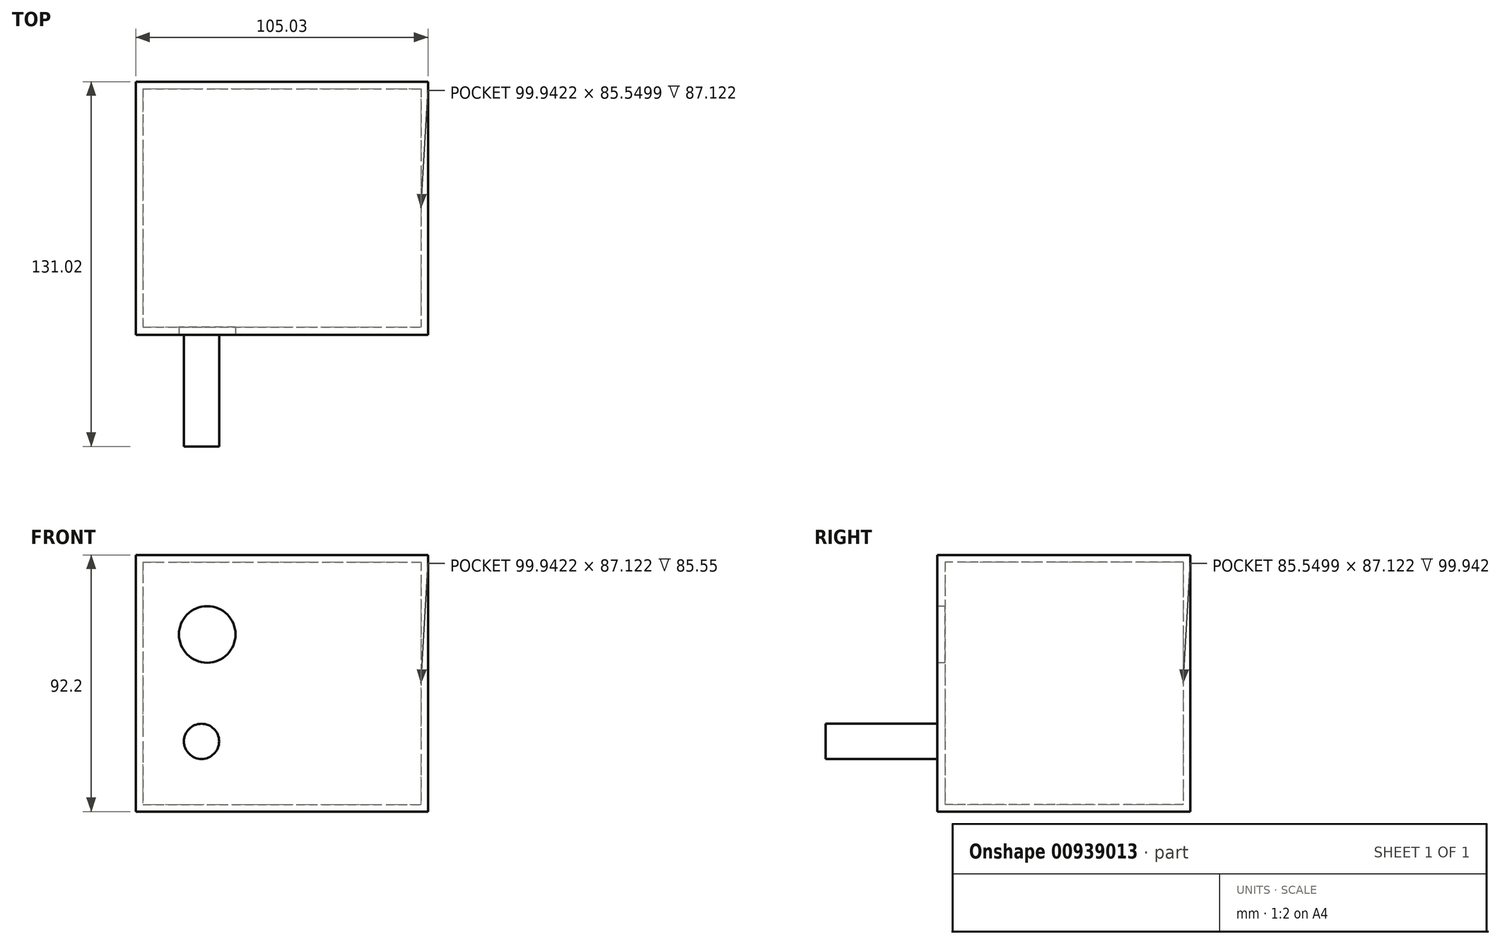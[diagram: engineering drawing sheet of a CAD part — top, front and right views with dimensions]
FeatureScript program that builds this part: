
annotation { "Feature Type Name" : "Feature", "Feature Type Description" : "" }
export const myFeature = defineFeature(function(context is Context, id is Id, definition is map)
    precondition{}
    {
        {
            var Q0;
            Q0=qCreatedBy(makeId("Top.planeOp"),FACE);
            var sketch = newSketch(context, id + "F0", { "sketchPlane" : qUnion([Q0])});
            skLineSegment(sketch, "E0.bottom", {"start": v(-76.02, 23.42) * mm, "end": v(29, 23.42) * mm});
            skLineSegment(sketch, "E0.top", {"start": v(-76.02, -67.46) * mm, "end": v(29, -67.46) * mm});
            skLineSegment(sketch, "E0.left", {"start": v(-76.02, 23.42) * mm, "end": v(-76.02, -67.46) * mm});
            skLineSegment(sketch, "E0.right", {"start": v(29, 23.42) * mm, "end": v(29, -67.46) * mm});
            skSolve(sketch);
        }
        {
            var Q0;
            Q0=makeQuery(id+"F0.imprint","IMPRINT",FACE,{"disambiguationData":[TD([[makeQuery(id+"F0.imprint","IMPRINT",EDGE,{"derivedFrom":sQuery(id+"F0.wireOp",EDGE,"E0.bottom")}),-1.0]])]});
            extrude(context, id + "F1", {"entities" : qUnion([Q0]), "depth" : 92.2 * mm, "offsetDistance" : 25.4 * mm});
        }
        {
            var Q0;
            Q0=makeQuery(id+"F1.opExtrude","SWEPT_FACE",FACE,{"disambiguationData":[OSD([sQuery(id+"F0.wireOp",EDGE,"E0.top")])]});
            shell(context, id + "F2", {"entities" : qUnion([Q0]), "thickness" : 2.54 * mm});
        }
        {
            var Q0;
            Q0=makeQuery(id+"F1.opExtrude","SWEPT_FACE",FACE,{"disambiguationData":[OSD([sQuery(id+"F0.wireOp",EDGE,"E0.top")])]});
            var sketch = newSketch(context, id + "F3", { "sketchPlane" : qUnion([Q0])});
            skLineSegment(sketch, "E1.bottom", {"start": v(-73.48, 89.66) * mm, "end": v(26.47, 89.66) * mm});
            skLineSegment(sketch, "E1.top", {"start": v(-73.48, 2.54) * mm, "end": v(26.47, 2.54) * mm});
            skLineSegment(sketch, "E1.left", {"start": v(-73.48, 89.66) * mm, "end": v(-73.48, 2.54) * mm});
            skLineSegment(sketch, "E1.right", {"start": v(26.47, 89.66) * mm, "end": v(26.47, 2.54) * mm});
            skSolve(sketch);
        }
        {
            var Q0;
            Q0=makeQuery(id+"F3.imprint","IMPRINT",FACE,{"disambiguationData":[TD([[makeQuery(id+"F3.imprint","IMPRINT",EDGE,{"derivedFrom":sQuery(id+"F3.wireOp",EDGE,"E1.bottom")}),-1.0]])]});
            extrude(context, id + "F4", {"entities" : qUnion([Q0]), "operationType" : NewBodyOperationType.ADD, "oppositeDirection" : true, "depth" : 2.8 * mm, "offsetDistance" : 25.4 * mm});
        }
        {
            var Q0;
            Q0=makeQuery(id+"F4.boolean.opBoolean","MERGE",FACE,{"derivedFrom":[makeQuery(id+"F1.opExtrude","SWEPT_FACE",FACE,{"disambiguationData":[OSD([sQuery(id+"F0.wireOp",EDGE,"E0.top")])]}),makeQuery(id+"F4.opExtrude","CAP_FACE",FACE,{"disambiguationData":[OSD([sQuery(id+"F3.wireOp",EDGE,"E1.bottom"),sQuery(id+"F3.wireOp",EDGE,"E1.top"),sQuery(id+"F3.wireOp",EDGE,"E1.left"),sQuery(id+"F3.wireOp",EDGE,"E1.right")])],"isStart":true})]});
            var sketch = newSketch(context, id + "F5", { "sketchPlane" : qUnion([Q0])});
            skCircle(sketch, "E2", {"center": v(-50.33, 63.63) * mm, "radius": 12.12 * mm});
            skSolve(sketch);
        }
        {
            var Q0;
            Q0=sQuery(id+"F5.wireOp",VERTEX,"E2.center");
            var Q1;
            Q1=makeQuery(id+"F1.opExtrude","SWEPT_BODY",BODY,{"disambiguationData":[OSD([sQuery(id+"F0.wireOp",EDGE,"E0.bottom"),sQuery(id+"F0.wireOp",EDGE,"E0.top"),sQuery(id+"F0.wireOp",EDGE,"E0.left"),sQuery(id+"F0.wireOp",EDGE,"E0.right")])]});
            hole(context, id + "F6", {"style" : HoleStyle.SIMPLE, "endStyle" : HoleEndStyle.BLIND, "holeDiameter" : 20.32 * mm, "majorDiameter" : 6.35 * mm, "holeDepth" : 20.32 * mm, "isTappedThrough" : true, "tappedDepth" : 12.7 * mm, "tapClearance" : 3, "locations" : qUnion([Q0]), "scope" : qUnion([Q1])});
        }
        {
            var Q0;
            Q0=makeQuery(id+"F4.boolean.opBoolean","MERGE",FACE,{"derivedFrom":[makeQuery(id+"F1.opExtrude","SWEPT_FACE",FACE,{"disambiguationData":[OSD([sQuery(id+"F0.wireOp",EDGE,"E0.top")])]}),makeQuery(id+"F4.opExtrude","CAP_FACE",FACE,{"disambiguationData":[OSD([sQuery(id+"F3.wireOp",EDGE,"E1.bottom"),sQuery(id+"F3.wireOp",EDGE,"E1.top"),sQuery(id+"F3.wireOp",EDGE,"E1.left"),sQuery(id+"F3.wireOp",EDGE,"E1.right")])],"isStart":true})]});
            var sketch = newSketch(context, id + "F7", { "sketchPlane" : qUnion([Q0])});
            skCircle(sketch, "E3", {"center": v(-52.37, 25.21) * mm, "radius": 6.31 * mm});
            skSolve(sketch);
        }
        {
            var Q0;
            Q0=makeQuery(id+"F7.imprint","IMPRINT",FACE,{"disambiguationData":[TD([[makeQuery(id+"F7.imprint","IMPRINT",EDGE,{"derivedFrom":sQuery(id+"F7.wireOp",EDGE,"E3")}),1.0]])]});
            extrude(context, id + "F8", {"entities" : qUnion([Q0]), "operationType" : NewBodyOperationType.ADD, "depth" : 40.13 * mm, "offsetDistance" : 25.4 * mm});
        }
    });
